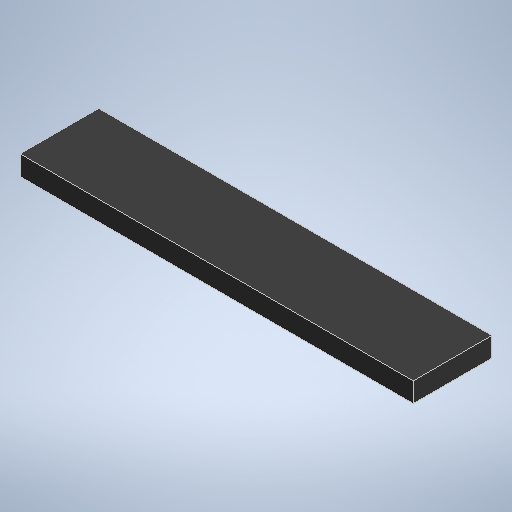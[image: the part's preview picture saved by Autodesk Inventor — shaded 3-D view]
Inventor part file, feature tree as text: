
AUTODESK INVENTOR PART (.ipt)
format: ipt  version: 2025 (Build 290162010, 162A)  size: 232,448 bytes
history: native  units: mm
features: extrude x1, sketch x1
ambient origin geometry x8: Origin, YZ Plane, XZ Plane, XY Plane, X Axis, Y Axis, Z Axis, Center Point
bodies: Volumenkörper1 (feature_tree)
feature tree (2):
  extrude  "Extrusion1"  Depth=4.0mm
  sketch  "Skizze1"  dims[d0=20.0mm d1=4.0mm d2=1.0mm d3=0.0mm]
